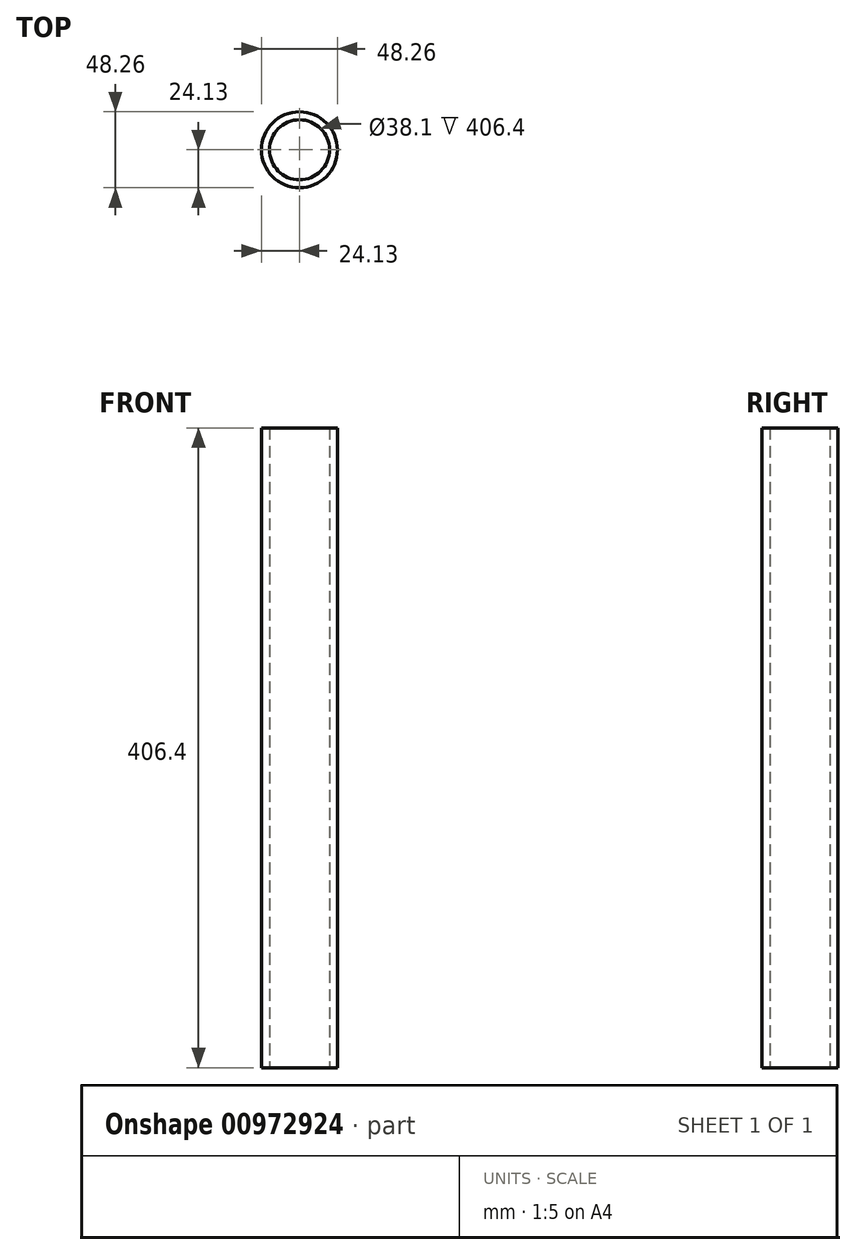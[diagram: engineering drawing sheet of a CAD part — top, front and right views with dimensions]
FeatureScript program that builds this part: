
annotation { "Feature Type Name" : "Feature", "Feature Type Description" : "" }
export const myFeature = defineFeature(function(context is Context, id is Id, definition is map)
    precondition{}
    {
        {
            var Q0;
            Q0=qCreatedBy(makeId("Top.planeOp"),FACE);
            var sketch = newSketch(context, id + "F0", { "sketchPlane" : qUnion([Q0])});
            skCircle(sketch, "E0", {"center": v(0, 0) * mm, "radius": 19.05 * mm});
            skCircle(sketch, "E1", {"center": v(0, 0) * mm, "radius": 24.13 * mm});
            skSolve(sketch);
        }
        {
            var Q0;
            Q0=makeQuery(id+"F0.imprint","IMPRINT",FACE,{"disambiguationData":[TD([[makeQuery(id+"F0.imprint","IMPRINT",EDGE,{"derivedFrom":sQuery(id+"F0.wireOp",EDGE,"E0")}),-1.0]])]});
            extrude(context, id + "F1", {"entities" : qUnion([Q0]), "depth" : 406.4 * mm, "offsetDistance" : 25.4 * mm});
        }
    });
